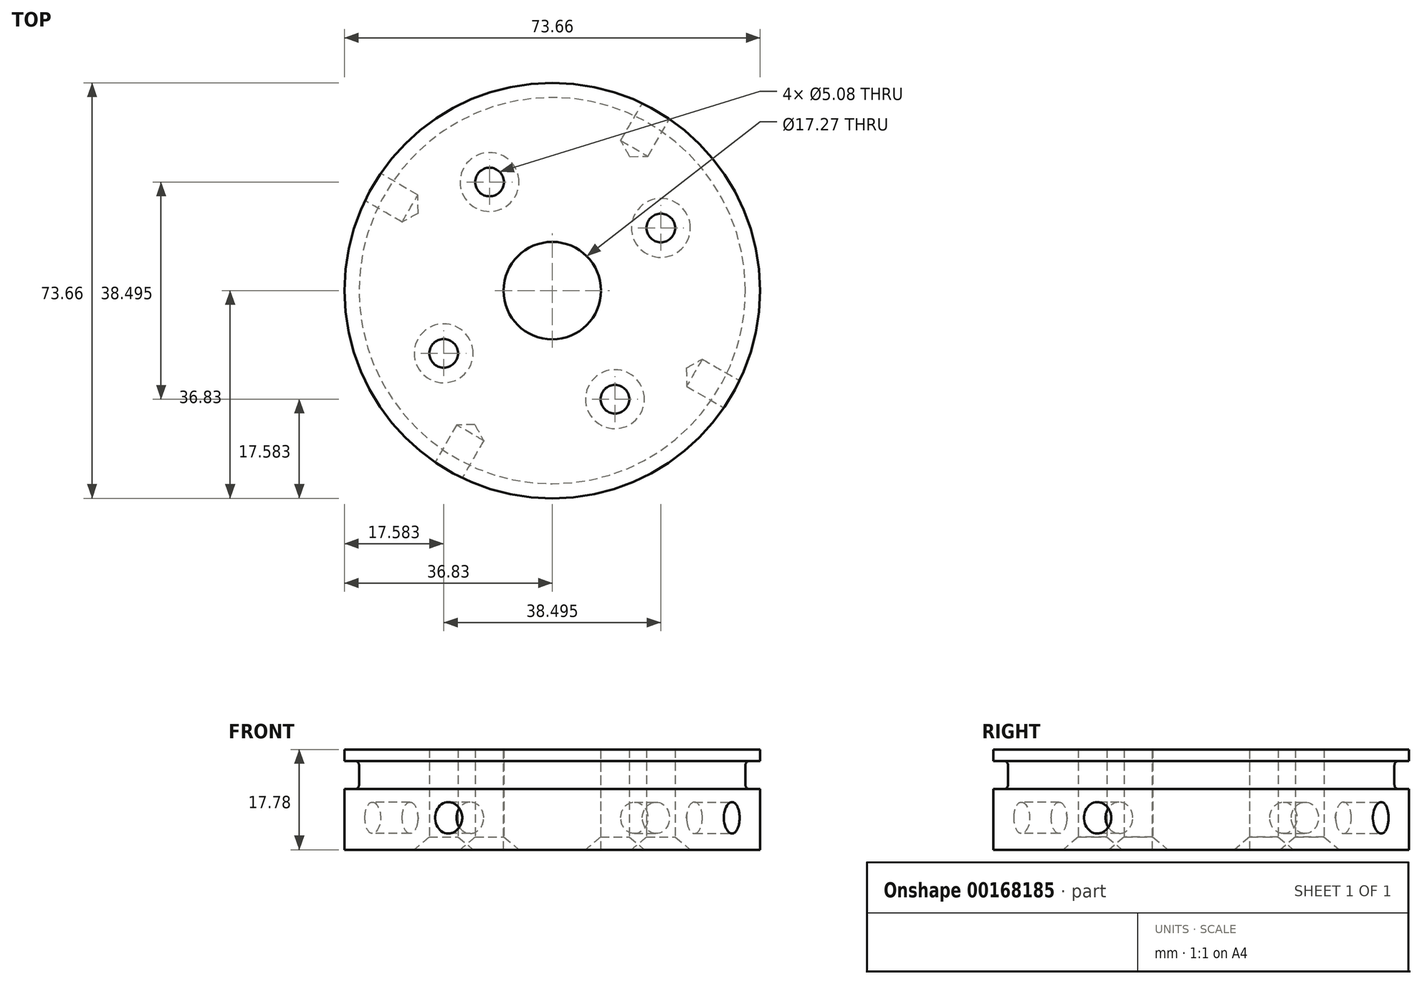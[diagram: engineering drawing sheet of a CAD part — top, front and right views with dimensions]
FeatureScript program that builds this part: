
annotation { "Feature Type Name" : "Feature", "Feature Type Description" : "" }
export const myFeature = defineFeature(function(context is Context, id is Id, definition is map)
    precondition{}
    {
        {
            var Q0;
            Q0=qCreatedBy(makeId("Top.planeOp"),FACE);
            var sketch = newSketch(context, id + "F0", { "sketchPlane" : qUnion([Q0])});
            skCircle(sketch, "E0", {"center": v(0, 0) * mm, "radius": 36.83 * mm});
            skSolve(sketch);
        }
        {
            var Q0;
            Q0=makeQuery(id+"F0.imprint","IMPRINT",FACE,{"disambiguationData":[TD([[makeQuery(id+"F0.imprint","IMPRINT",EDGE,{"derivedFrom":sQuery(id+"F0.wireOp",EDGE,"E0")}),1.0]])]});
            extrude(context, id + "F1", {"entities" : qUnion([Q0]), "depth" : 17.78 * mm});
        }
        {
            var Q0;
            Q0=makeQuery(id+"FNZgXB3MDCEPfWC_1.boolean.opBoolean","SPLIT",FACE,{"disambiguationData":[TD([makeQuery(id+"FNZgXB3MDCEPfWC_1.opExtrude","SWEPT_FACE",FACE,{"disambiguationData":[OSD([sQuery(id+"FiLk9hSRQ8Dv81E_1.wireOp",EDGE,"Xvq2NHEn-EDZK-GzOR-rNrk-moL4fFsD4KvI")])]})])],"derivedFrom":makeQuery(id+"F1.opExtrude","CAP_FACE",FACE,{"disambiguationData":[OSD([sQuery(id+"F0.wireOp",EDGE,"E0")])],"isStart":false})});
            var sketch = newSketch(context, id + "F2", { "sketchPlane" : qUnion([Q0])});
            skCircle(sketch, "E1", {"center": v(0, 0) * mm, "radius": 8.64 * mm});
            skSolve(sketch);
        }
        {
            var Q0;
            Q0=qSketchRegion(id+"F2",true);
            extrude(context, id + "F3", {"entities" : qUnion([Q0]), "operationType" : NewBodyOperationType.REMOVE, "endBound" : BoundingType.THROUGH_ALL, "oppositeDirection" : true, "depth" : 25.4 * mm});
        }
        {
            var Q0;
            Q0=makeQuery(id+"FOQC5dfjhO448EJ_1.boolean.opBoolean","SPLIT",FACE,{"disambiguationData":[TD([makeQuery(id+"F3.boolean.opBoolean","COPY",FACE,{"derivedFrom":makeQuery(id+"F3.opExtrude","SWEPT_FACE",FACE,{"disambiguationData":[OSD([sQuery(id+"F2.wireOp",EDGE,"E1")])]})})])],"derivedFrom":makeQuery(id+"F1.opExtrude","CAP_FACE",FACE,{"disambiguationData":[OSD([sQuery(id+"F0.wireOp",EDGE,"E0")])],"isStart":false})});
            cPlane(context, id + "F4", {"entities" : qUnion([Q0]), "cplaneType" : CPlaneType.OFFSET, "offset" : 2.03 * mm, "oppositeDirection" : true, "width" : 152.4 * mm, "height" : 152.4 * mm});
        }
        {
            var Q0;
            Q0=qCreatedBy(id+"F4.planeOp",FACE);
            var sketch = newSketch(context, id + "F5", { "sketchPlane" : qUnion([Q0])});
            skCircle(sketch, "E2", {"center": v(0, 0) * mm, "radius": 34.24 * mm});
            skCircle(sketch, "E3.0", {"center": v(0, 0) * mm, "radius": 36.83 * mm});
            skSolve(sketch);
        }
        {
            var Q0;
            Q0=qSketchRegion(id+"F5",true);
            extrude(context, id + "F6", {"entities" : qUnion([Q0]), "operationType" : NewBodyOperationType.REMOVE, "oppositeDirection" : true, "depth" : 5 * mm});
        }
        {
            var Q0;
            Q0=makeQuery(id+"F6.boolean.opBoolean","COPY",EDGE,{"derivedFrom":makeQuery(id+"F6.opExtrude","CAP_EDGE",EDGE,{"disambiguationData":[OSD([sQuery(id+"F5.wireOp",EDGE,"E2")])],"isStart":false})});
            var Q1;
            Q1=makeQuery(id+"F6.boolean.opBoolean","COPY",EDGE,{"derivedFrom":makeQuery(id+"F6.opExtrude","CAP_EDGE",EDGE,{"disambiguationData":[OSD([sQuery(id+"F5.wireOp",EDGE,"E2")])],"isStart":true})});
            fillet(context, id + "F7", {"entities" : qUnion([Q0, Q1]), "radius" : 0.76 * mm, "tangentPropagation" : true, "allowEdgeOverflow" : false});
        }
        {
            var Q0;
            {var subQ1=sQuery(id+"F0.wireOp",EDGE,"E0");var subQ2=makeQuery(id+"F1.opExtrude","SWEPT_FACE",FACE,{"disambiguationData":[OSD([subQ1])]});Q0=makeQuery(id+"FkcieFRIapZdHPD_1.boolean.opBoolean","SPLIT",FACE,{"disambiguationData":[TD([subQ2])],"derivedFrom":makeQuery(id+"F1.opExtrude","CAP_FACE",FACE,{"disambiguationData":[OSD([subQ1])],"isStart":false})});}
            var sketch = newSketch(context, id + "F8", { "sketchPlane" : qUnion([Q0])});
            skCircle(sketch, "E4.0", {"center": v(0, 0) * mm, "radius": 36.83 * mm, "construction": true});
            skPoint(sketch, "E5", {"position": v(-18.41, -31.9) * mm});
            skLineSegment(sketch, "E6", {"start": v(0, -36.83) * mm, "end": v(0, 0) * mm, "construction": true});
            skLineSegment(sketch, "E7", {"start": v(0, 0) * mm, "end": v(-17.96, -31.1) * mm, "construction": true});
            skLineSegment(sketch, "E8", {"start": v(-17.96, -31.1) * mm, "end": v(-18.41, -31.9) * mm, "construction": true});
            skLineSegment(sketch, "E9", {"start": v(0, 0) * mm, "end": v(18.41, 31.9) * mm, "construction": true});
            skLineSegment(sketch, "E10", {"start": v(18.41, 31.9) * mm, "end": v(0, 0) * mm, "construction": true});
            skLineSegment(sketch, "E11", {"start": v(31.9, -18.41) * mm, "end": v(0, 0) * mm, "construction": true});
            skLineSegment(sketch, "E12", {"start": v(0, 0) * mm, "end": v(-31.9, 18.41) * mm, "construction": true});
            skPoint(sketch, "E13", {"position": v(18.41, 31.9) * mm});
            skPoint(sketch, "E14", {"position": v(31.9, -18.41) * mm});
            skPoint(sketch, "E15", {"position": v(-31.9, 18.41) * mm});
            skSolve(sketch);
        }
        {
            var Q0;
            Q0=qCreatedBy(makeId("Front.planeOp"),FACE);
            var sketch = newSketch(context, id + "F9", { "sketchPlane" : qUnion([Q0])});
            skLineSegment(sketch, "E16", {"start": v(0, 0) * mm, "end": v(0, 38.57) * mm, "construction": true});
            skSolve(sketch);
        }
        {
            var Q0;
            Q0=sQuery(id+"F9.wireOp",EDGE,"E16");
            cPlane(context, id + "F10", {"entities" : qUnion([Q0]), "cplaneType" : CPlaneType.LINE_ANGLE, "offset" : 25.4 * mm, "angle" : 60 * degree, "width" : 152.4 * mm, "height" : 152.4 * mm});
        }
        {
            var Q0;
            Q0=sQuery(id+"F8.wireOp",VERTEX,"E5");
            var Q1;
            Q1=qCreatedBy(id+"F10.planeOp",FACE);
            cPlane(context, id + "F11", {"entities" : qUnion([Q0, Q1]), "cplaneType" : CPlaneType.PLANE_POINT, "offset" : 25.4 * mm, "width" : 152.4 * mm, "height" : 152.4 * mm});
        }
        {
            var Q0;
            Q0=qCreatedBy(id+"F11.planeOp",FACE);
            var Q1;
            Q1=sQuery(id+"F8.wireOp",VERTEX,"E13");
            cPlane(context, id + "F12", {"entities" : qUnion([Q0, Q1]), "cplaneType" : CPlaneType.PLANE_POINT, "offset" : 25.4 * mm, "width" : 152.4 * mm, "height" : 152.4 * mm});
        }
        {
            var Q0;
            Q0=sQuery(id+"F9.wireOp",EDGE,"E16");
            cPlane(context, id + "F13", {"entities" : qUnion([Q0]), "cplaneType" : CPlaneType.LINE_ANGLE, "offset" : 25.4 * mm, "angle" : 150 * degree, "width" : 152.4 * mm, "height" : 152.4 * mm});
        }
        {
            var Q0;
            Q0=sQuery(id+"F8.wireOp",VERTEX,"E15");
            var Q1;
            Q1=qCreatedBy(id+"F13.planeOp",FACE);
            cPlane(context, id + "F14", {"entities" : qUnion([Q0, Q1]), "cplaneType" : CPlaneType.PLANE_POINT, "offset" : 25.4 * mm, "width" : 152.4 * mm, "height" : 152.4 * mm});
        }
        {
            var Q0;
            Q0=qCreatedBy(id+"F13.planeOp",FACE);
            var Q1;
            Q1=sQuery(id+"F8.wireOp",VERTEX,"E14");
            cPlane(context, id + "F15", {"entities" : qUnion([Q0, Q1]), "cplaneType" : CPlaneType.PLANE_POINT, "offset" : 25.4 * mm, "width" : 152.4 * mm, "height" : 152.4 * mm});
        }
        {
            var Q0;
            Q0=qCreatedBy(id+"F11.planeOp",FACE);
            var sketch = newSketch(context, id + "F16", { "sketchPlane" : qUnion([Q0])});
            skLineSegment(sketch, "E17", {"start": v(0, 0) * mm, "end": v(0, 5.66) * mm, "construction": true});
            skPoint(sketch, "E18", {"position": v(0, 5.66) * mm});
            skSolve(sketch);
        }
        {
            var Q0;
            Q0=qCreatedBy(id+"F12.planeOp",FACE);
            var sketch = newSketch(context, id + "F17", { "sketchPlane" : qUnion([Q0])});
            skPoint(sketch, "E19", {"position": v(0, 5.66) * mm});
            skLineSegment(sketch, "E20.0", {"start": v(0, 0) * mm, "end": v(0, 5.66) * mm, "construction": true});
            skSolve(sketch);
        }
        {
            var Q0;
            Q0=qCreatedBy(id+"F14.planeOp",FACE);
            var sketch = newSketch(context, id + "F18", { "sketchPlane" : qUnion([Q0])});
            skLineSegment(sketch, "E21", {"start": v(0, 0) * mm, "end": v(0, 5.66) * mm, "construction": true});
            skLineSegment(sketch, "E22.0", {"start": v(-36.83, 0) * mm, "end": v(-36.83, 5.66) * mm, "construction": true});
            skPoint(sketch, "E23", {"position": v(0, 5.66) * mm});
            skLineSegment(sketch, "E24", {"start": v(-36.83, 5.66) * mm, "end": v(0, 5.66) * mm, "construction": true});
            skSolve(sketch);
        }
        {
            var Q0;
            Q0=qCreatedBy(id+"F15.planeOp",FACE);
            var sketch = newSketch(context, id + "F19", { "sketchPlane" : qUnion([Q0])});
            skLineSegment(sketch, "E25.0", {"start": v(0, 0) * mm, "end": v(0, 5.66) * mm, "construction": true});
            skPoint(sketch, "E26", {"position": v(0, 5.66) * mm});
            skSolve(sketch);
        }
        {
            var Q0;
            Q0=sQuery(id+"F19.wireOp",VERTEX,"E26");
            var Q1;
            Q1=makeQuery(id+"F1.opExtrude","SWEPT_BODY",BODY,{"disambiguationData":[OSD([sQuery(id+"F0.wireOp",EDGE,"E0")])]});
            hole(context, id + "F20", {"style" : HoleStyle.SIMPLE, "endStyle" : HoleEndStyle.BLIND, "oppositeDirection" : true, "standardTappedOrClearance" : lookupTablePath({ "standard" : "ANSI", "engagement" : "75%", "pitch" : "32 tpi", "size" : "1/4", "type" : "Tapped" }), "standardBlindInLast" : lookupTablePath({ "standard" : "ANSI", "engagement" : "75%", "pitch" : "32 tpi", "size" : "1/4", "type" : "Tapped" }), "holeDiameter" : 5.56 * mm, "holeDepth" : 7.62 * mm, "locations" : qUnion([Q0]), "scope" : qUnion([Q1]), "majorDiameter" : 6.35 * mm});
        }
        {
            var Q0;
            Q0=sQuery(id+"F18.wireOp",VERTEX,"E23");
            var Q1;
            Q1=makeQuery(id+"F1.opExtrude","SWEPT_BODY",BODY,{"disambiguationData":[OSD([sQuery(id+"F0.wireOp",EDGE,"E0")])]});
            hole(context, id + "F21", {"style" : HoleStyle.SIMPLE, "endStyle" : HoleEndStyle.BLIND, "standardTappedOrClearance" : lookupTablePath({ "standard" : "ANSI", "engagement" : "75%", "pitch" : "32 tpi", "size" : "1/4", "type" : "Tapped" }), "standardBlindInLast" : lookupTablePath({ "standard" : "ANSI", "engagement" : "75%", "pitch" : "32 tpi", "size" : "1/4", "type" : "Tapped" }), "holeDiameter" : 5.56 * mm, "holeDepth" : 7.62 * mm, "locations" : qUnion([Q0]), "scope" : qUnion([Q1]), "majorDiameter" : 6.35 * mm});
        }
        {
            var Q0;
            Q0=sQuery(id+"F16.wireOp",VERTEX,"E18");
            var Q1;
            Q1=makeQuery(id+"F1.opExtrude","SWEPT_BODY",BODY,{"disambiguationData":[OSD([sQuery(id+"F0.wireOp",EDGE,"E0")])]});
            hole(context, id + "F22", {"style" : HoleStyle.SIMPLE, "endStyle" : HoleEndStyle.BLIND, "oppositeDirection" : true, "standardTappedOrClearance" : lookupTablePath({ "standard" : "ANSI", "engagement" : "75%", "pitch" : "32 tpi", "size" : "1/4", "type" : "Tapped" }), "standardBlindInLast" : lookupTablePath({ "standard" : "ANSI", "engagement" : "75%", "pitch" : "32 tpi", "size" : "1/4", "type" : "Tapped" }), "holeDiameter" : 5.56 * mm, "holeDepth" : 7.62 * mm, "locations" : qUnion([Q0]), "scope" : qUnion([Q1]), "majorDiameter" : 6.35 * mm});
        }
        {
            var Q0;
            Q0=sQuery(id+"F17.wireOp",VERTEX,"E19");
            var Q1;
            Q1=makeQuery(id+"F1.opExtrude","SWEPT_BODY",BODY,{"disambiguationData":[OSD([sQuery(id+"F0.wireOp",EDGE,"E0")])]});
            hole(context, id + "F23", {"style" : HoleStyle.SIMPLE, "endStyle" : HoleEndStyle.BLIND, "standardTappedOrClearance" : lookupTablePath({ "standard" : "ANSI", "engagement" : "75%", "pitch" : "32 tpi", "size" : "1/4", "type" : "Tapped" }), "standardBlindInLast" : lookupTablePath({ "standard" : "ANSI", "engagement" : "75%", "pitch" : "32 tpi", "size" : "1/4", "type" : "Tapped" }), "holeDiameter" : 5.56 * mm, "holeDepth" : 7.62 * mm, "locations" : qUnion([Q0]), "scope" : qUnion([Q1]), "majorDiameter" : 6.35 * mm});
        }
        {
            var Q0;
            Q0=makeQuery(id+"F1.opExtrude","CAP_FACE",FACE,{"disambiguationData":[OSD([sQuery(id+"F0.wireOp",EDGE,"E0")])],"isStart":true});
            var sketch = newSketch(context, id + "F24", { "sketchPlane" : qUnion([Q0])});
            skLineSegment(sketch, "E27", {"start": v(0, 0) * mm, "end": v(-11.11, -19.25) * mm, "construction": true});
            skPoint(sketch, "E28", {"position": v(-11.11, -19.25) * mm});
            skPoint(sketch, "E29.1.0", {"position": v(19.25, -11.11) * mm});
            skPoint(sketch, "E29.2.0", {"position": v(11.11, 19.25) * mm});
            skPoint(sketch, "E29.3.0", {"position": v(-19.25, 11.11) * mm});
            skPoint(sketch, "E29.center", {"position": v(0, 0) * mm});
            skSolve(sketch);
        }
        {
            var Q0;
            Q0=sQuery(id+"F24.wireOp",VERTEX,"E29.3.0");
            var Q1;
            Q1=sQuery(id+"F24.wireOp",VERTEX,"E28");
            var Q2;
            Q2=sQuery(id+"F24.wireOp",VERTEX,"E29.1.0");
            var Q3;
            Q3=sQuery(id+"F24.wireOp",VERTEX,"E29.2.0");
            var Q4;
            Q4=makeQuery(id+"F1.opExtrude","SWEPT_BODY",BODY,{"disambiguationData":[OSD([sQuery(id+"F0.wireOp",EDGE,"E0")])]});
            hole(context, id + "F25", {"style" : HoleStyle.C_SINK, "endStyle" : HoleEndStyle.THROUGH, "holeDiameter" : 5.08 * mm, "cSinkDiameter" : 10.44 * mm, "cSinkAngle" : 100 * degree, "locations" : qUnion([Q0, Q1, Q2, Q3]), "scope" : qUnion([Q4]), "isTappedThrough" : true});
        }
    });
